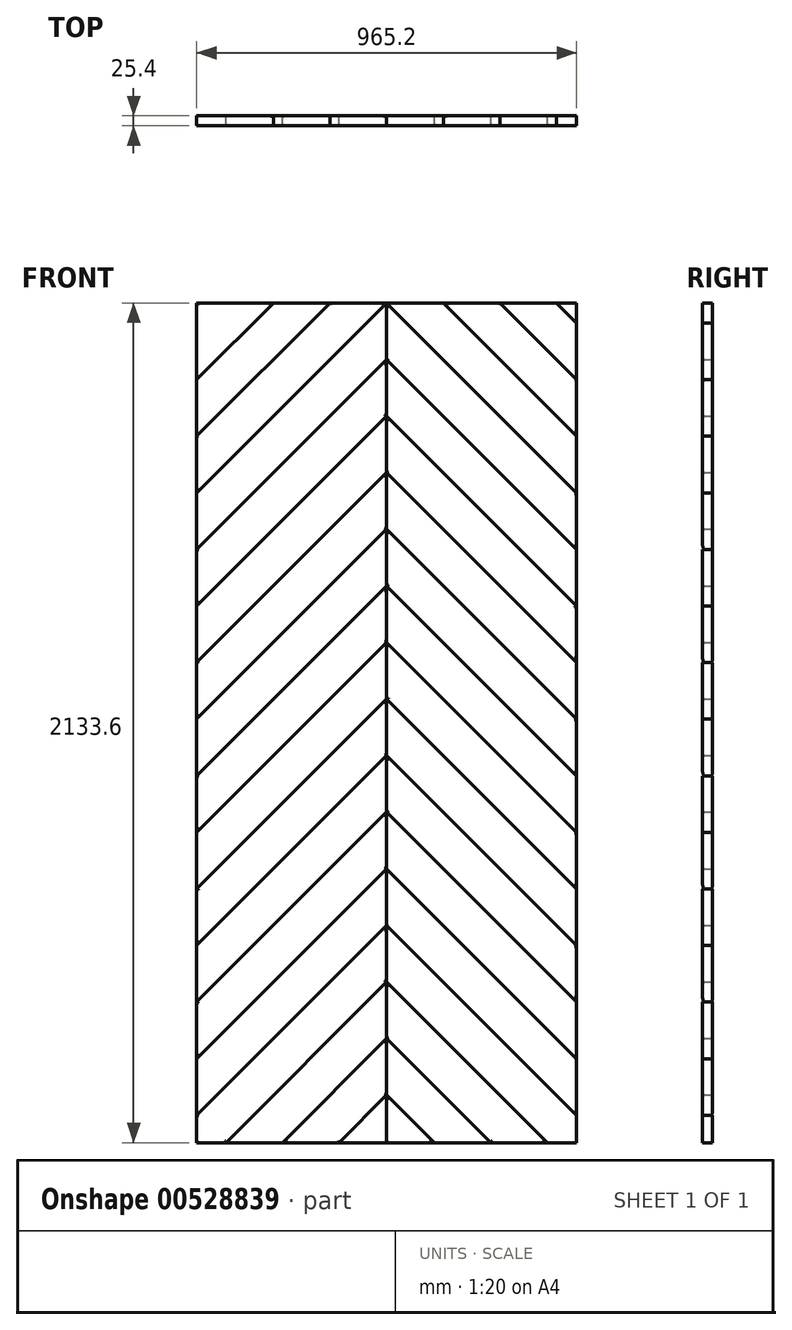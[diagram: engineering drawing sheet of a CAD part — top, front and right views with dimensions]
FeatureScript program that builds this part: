
annotation { "Feature Type Name" : "Feature", "Feature Type Description" : "" }
export const myFeature = defineFeature(function(context is Context, id is Id, definition is map)
    precondition{}
    {
        {
            var Q0;
            Q0=qCreatedBy(makeId("Front.planeOp"),FACE);
            var sketch = newSketch(context, id + "F0", { "sketchPlane" : qUnion([Q0])});
            skLineSegment(sketch, "E0.bottom", {"start": v(482.6, -1066.8) * mm, "end": v(0, -1066.8) * mm});
            skLineSegment(sketch, "E0.top", {"start": v(482.6, 1066.8) * mm, "end": v(0, 1066.8) * mm});
            skLineSegment(sketch, "E0.left", {"start": v(482.6, -1066.8) * mm, "end": v(482.6, 1066.8) * mm});
            skLineSegment(sketch, "E0.right", {"start": v(-482.6, -1066.8) * mm, "end": v(-482.6, 1066.8) * mm});
            skPoint(sketch, "E0.middle", {"position": v(0, 0) * mm});
            skLineSegment(sketch, "E1", {"start": v(0, 1066.8) * mm, "end": v(-482.6, 1066.8) * mm});
            skLineSegment(sketch, "E2", {"start": v(0, -1066.8) * mm, "end": v(-482.6, -1066.8) * mm});
            skLineSegment(sketch, "E3", {"start": v(0, 1066.8) * mm, "end": v(0, -1066.8) * mm});
            skLineSegment(sketch, "E4", {"start": v(0, 1066.8) * mm, "end": v(-482.6, 584.2) * mm});
            skLineSegment(sketch, "E5.1.0.0", {"start": v(0, 923.04) * mm, "end": v(-482.6, 440.44) * mm});
            skLineSegment(sketch, "E5.2.0.0", {"start": v(0, 779.27) * mm, "end": v(-482.6, 296.67) * mm});
            skLineSegment(sketch, "E5.3.0.0", {"start": v(0, 635.5) * mm, "end": v(-482.6, 152.9) * mm});
            skLineSegment(sketch, "E5.4.0.0", {"start": v(0, 491.74) * mm, "end": v(-482.6, 9.14) * mm});
            skLineSegment(sketch, "E5.5.0.0", {"start": v(0, 347.98) * mm, "end": v(-482.6, -134.62) * mm});
            skLineSegment(sketch, "E5.6.0.0", {"start": v(0, 204.22) * mm, "end": v(-482.6, -278.38) * mm});
            skLineSegment(sketch, "E5.7.0.0", {"start": v(0, 60.45) * mm, "end": v(-482.6, -422.15) * mm});
            skLineSegment(sketch, "E5.8.0.0", {"start": v(0, -83.31) * mm, "end": v(-482.6, -565.91) * mm});
            skLineSegment(sketch, "E5.9.0.0", {"start": v(0, -227.08) * mm, "end": v(-482.6, -709.68) * mm});
            skLineSegment(sketch, "E5.10.0.0", {"start": v(0, -370.84) * mm, "end": v(-482.6, -853.44) * mm});
            skLineSegment(sketch, "E5.11.0.0", {"start": v(0, -514.6) * mm, "end": v(-482.6, -997.2) * mm});
            skLineSegment(sketch, "E5.12.0.0", {"start": v(0, -658.37) * mm, "end": v(-408.43, -1066.8) * mm});
            skLineSegment(sketch, "E5.13.0.0", {"start": v(0, -802.13) * mm, "end": v(-264.67, -1066.8) * mm});
            skLineSegment(sketch, "E5.14.0.0", {"start": v(0, -945.9) * mm, "end": v(-120.9, -1066.8) * mm});
            skLineSegment(sketch, "E5.direction1", {"start": v(-482.6, 584.2) * mm, "end": v(-482.6, 440.44) * mm, "construction": true});
            skPoint(sketch, "E6.orphan", {"position": v(-482.6, -1428.5) * mm});
            skPoint(sketch, "E7.orphan", {"position": v(-482.6, -1284.73) * mm});
            skPoint(sketch, "E8.orphan", {"position": v(-482.6, -1140.97) * mm});
            skLineSegment(sketch, "E9.1.0.0", {"start": v(-143.76, 1066.8) * mm, "end": v(-482.6, 727.96) * mm});
            skLineSegment(sketch, "E9.2.0.0", {"start": v(-287.53, 1066.8) * mm, "end": v(-482.6, 871.73) * mm});
            skLineSegment(sketch, "E9.3.0.0", {"start": v(-431.3, 1066.8) * mm, "end": v(-482.6, 1015.5) * mm});
            skLineSegment(sketch, "E9.direction1", {"start": v(-482.6, 584.2) * mm, "end": v(-626.36, 584.2) * mm, "construction": true});
            skPoint(sketch, "E10.orphan", {"position": v(-913.9, 584.2) * mm});
            skPoint(sketch, "E11.orphan", {"position": v(-770.13, 584.2) * mm});
            skLineSegment(sketch, "E12", {"start": v(0, 1066.8) * mm, "end": v(482.6, 584.2) * mm});
            skLineSegment(sketch, "E13.1.0.0", {"start": v(143.76, 1066.8) * mm, "end": v(482.6, 727.96) * mm});
            skLineSegment(sketch, "E13.2.0.0", {"start": v(287.53, 1066.8) * mm, "end": v(482.6, 871.73) * mm});
            skLineSegment(sketch, "E13.3.0.0", {"start": v(431.3, 1066.8) * mm, "end": v(482.6, 1015.5) * mm});
            skLineSegment(sketch, "E13.direction1", {"start": v(0, 1066.8) * mm, "end": v(143.76, 1066.8) * mm, "construction": true});
            skPoint(sketch, "E14.orphan", {"position": v(913.9, 584.2) * mm});
            skPoint(sketch, "E15.orphan", {"position": v(770.13, 584.2) * mm});
            skPoint(sketch, "E16.orphan", {"position": v(626.36, 584.2) * mm});
            skLineSegment(sketch, "E17.1.0.0", {"start": v(0, 923.04) * mm, "end": v(482.6, 440.44) * mm});
            skLineSegment(sketch, "E17.2.0.0", {"start": v(0, 779.27) * mm, "end": v(482.6, 296.67) * mm});
            skLineSegment(sketch, "E17.3.0.0", {"start": v(0, 635.5) * mm, "end": v(482.6, 152.9) * mm});
            skLineSegment(sketch, "E17.4.0.0", {"start": v(0, 491.74) * mm, "end": v(482.6, 9.14) * mm});
            skLineSegment(sketch, "E17.5.0.0", {"start": v(0, 347.98) * mm, "end": v(482.6, -134.62) * mm});
            skLineSegment(sketch, "E17.6.0.0", {"start": v(0, 204.22) * mm, "end": v(482.6, -278.38) * mm});
            skLineSegment(sketch, "E17.7.0.0", {"start": v(0, 60.45) * mm, "end": v(482.6, -422.15) * mm});
            skLineSegment(sketch, "E17.8.0.0", {"start": v(0, -83.31) * mm, "end": v(482.6, -565.91) * mm});
            skLineSegment(sketch, "E17.9.0.0", {"start": v(0, -227.08) * mm, "end": v(482.6, -709.68) * mm});
            skLineSegment(sketch, "E17.10.0.0", {"start": v(0, -370.84) * mm, "end": v(482.6, -853.44) * mm});
            skLineSegment(sketch, "E17.11.0.0", {"start": v(0, -514.6) * mm, "end": v(482.6, -997.2) * mm});
            skLineSegment(sketch, "E17.12.0.0", {"start": v(0, -658.37) * mm, "end": v(408.43, -1066.8) * mm});
            skLineSegment(sketch, "E17.13.0.0", {"start": v(0, -802.13) * mm, "end": v(264.67, -1066.8) * mm});
            skLineSegment(sketch, "E17.14.0.0", {"start": v(0, -945.9) * mm, "end": v(120.9, -1066.8) * mm});
            skLineSegment(sketch, "E17.direction1", {"start": v(0, 1066.8) * mm, "end": v(0, 923.04) * mm, "construction": true});
            skPoint(sketch, "E18.orphan", {"position": v(482.6, -1428.5) * mm});
            skPoint(sketch, "E19.orphan", {"position": v(482.6, -1284.73) * mm});
            skPoint(sketch, "E20.orphan", {"position": v(482.6, -1140.97) * mm});
            skSolve(sketch);
        }
        {
            var Q0;
            {var subQ3=sQuery(id+"F0.wireOp",EDGE,"E9.3.0.0");Q0=makeQuery(id+"F0.imprint","IMPRINT",FACE,{"disambiguationData":[TD([[makeQuery(id+"F0.imprint","IMPRINT",EDGE,{"derivedFrom":subQ3}),-1.0]])]});}
            var Q1;
            {var subQ3=sQuery(id+"F0.wireOp",EDGE,"E13.3.0.0");Q1=makeQuery(id+"F0.imprint","IMPRINT",FACE,{"disambiguationData":[TD([[makeQuery(id+"F0.imprint","IMPRINT",EDGE,{"derivedFrom":subQ3}),1.0]])]});}
            var Q2;
            {var subQ3=sQuery(id+"F0.wireOp",EDGE,"E17.14.0.0");Q2=makeQuery(id+"F0.imprint","IMPRINT",FACE,{"disambiguationData":[TD([[makeQuery(id+"F0.imprint","IMPRINT",EDGE,{"derivedFrom":subQ3}),-1.0]])]});}
            var Q3;
            {var subQ0=sQuery(id+"F0.wireOp",EDGE,"E5.13.0.0");Q3=makeQuery(id+"F0.imprint","IMPRINT",FACE,{"disambiguationData":[TD([[makeQuery(id+"F0.imprint","IMPRINT",EDGE,{"derivedFrom":subQ0}),1.0]])]});}
            var Q4;
            {var subQ0=sQuery(id+"F0.wireOp",EDGE,"E17.12.0.0");Q4=makeQuery(id+"F0.imprint","IMPRINT",FACE,{"disambiguationData":[TD([[makeQuery(id+"F0.imprint","IMPRINT",EDGE,{"derivedFrom":subQ0}),-1.0]])]});}
            var Q5;
            {var subQ4=sQuery(id+"F0.wireOp",EDGE,"E5.11.0.0");Q5=makeQuery(id+"F0.imprint","IMPRINT",FACE,{"disambiguationData":[TD([[makeQuery(id+"F0.imprint","IMPRINT",EDGE,{"derivedFrom":subQ4}),1.0]])]});}
            var Q6;
            {var subQ0=sQuery(id+"F0.wireOp",EDGE,"E17.10.0.0");Q6=makeQuery(id+"F0.imprint","IMPRINT",FACE,{"disambiguationData":[TD([[makeQuery(id+"F0.imprint","IMPRINT",EDGE,{"derivedFrom":subQ0}),-1.0]])]});}
            var Q7;
            {var subQ0=sQuery(id+"F0.wireOp",EDGE,"E5.9.0.0");Q7=makeQuery(id+"F0.imprint","IMPRINT",FACE,{"disambiguationData":[TD([[makeQuery(id+"F0.imprint","IMPRINT",EDGE,{"derivedFrom":subQ0}),1.0]])]});}
            var Q8;
            {var subQ0=sQuery(id+"F0.wireOp",EDGE,"E17.8.0.0");Q8=makeQuery(id+"F0.imprint","IMPRINT",FACE,{"disambiguationData":[TD([[makeQuery(id+"F0.imprint","IMPRINT",EDGE,{"derivedFrom":subQ0}),-1.0]])]});}
            var Q9;
            {var subQ0=sQuery(id+"F0.wireOp",EDGE,"E5.7.0.0");Q9=makeQuery(id+"F0.imprint","IMPRINT",FACE,{"disambiguationData":[TD([[makeQuery(id+"F0.imprint","IMPRINT",EDGE,{"derivedFrom":subQ0}),1.0]])]});}
            var Q10;
            {var subQ0=sQuery(id+"F0.wireOp",EDGE,"E17.6.0.0");Q10=makeQuery(id+"F0.imprint","IMPRINT",FACE,{"disambiguationData":[TD([[makeQuery(id+"F0.imprint","IMPRINT",EDGE,{"derivedFrom":subQ0}),-1.0]])]});}
            var Q11;
            {var subQ0=sQuery(id+"F0.wireOp",EDGE,"E5.5.0.0");Q11=makeQuery(id+"F0.imprint","IMPRINT",FACE,{"disambiguationData":[TD([[makeQuery(id+"F0.imprint","IMPRINT",EDGE,{"derivedFrom":subQ0}),1.0]])]});}
            var Q12;
            {var subQ0=sQuery(id+"F0.wireOp",EDGE,"E17.4.0.0");Q12=makeQuery(id+"F0.imprint","IMPRINT",FACE,{"disambiguationData":[TD([[makeQuery(id+"F0.imprint","IMPRINT",EDGE,{"derivedFrom":subQ0}),-1.0]])]});}
            var Q13;
            {var subQ0=sQuery(id+"F0.wireOp",EDGE,"E5.3.0.0");Q13=makeQuery(id+"F0.imprint","IMPRINT",FACE,{"disambiguationData":[TD([[makeQuery(id+"F0.imprint","IMPRINT",EDGE,{"derivedFrom":subQ0}),1.0]])]});}
            var Q14;
            {var subQ0=sQuery(id+"F0.wireOp",EDGE,"E17.2.0.0");Q14=makeQuery(id+"F0.imprint","IMPRINT",FACE,{"disambiguationData":[TD([[makeQuery(id+"F0.imprint","IMPRINT",EDGE,{"derivedFrom":subQ0}),-1.0]])]});}
            var Q15;
            {var subQ0=sQuery(id+"F0.wireOp",EDGE,"E5.1.0.0");Q15=makeQuery(id+"F0.imprint","IMPRINT",FACE,{"disambiguationData":[TD([[makeQuery(id+"F0.imprint","IMPRINT",EDGE,{"derivedFrom":subQ0}),1.0]])]});}
            var Q16;
            {var subQ0=sQuery(id+"F0.wireOp",EDGE,"E12");Q16=makeQuery(id+"F0.imprint","IMPRINT",FACE,{"disambiguationData":[TD([[makeQuery(id+"F0.imprint","IMPRINT",EDGE,{"derivedFrom":subQ0}),-1.0]])]});}
            var Q17;
            {var subQ0=sQuery(id+"F0.wireOp",EDGE,"E4");Q17=makeQuery(id+"F0.imprint","IMPRINT",FACE,{"disambiguationData":[TD([[makeQuery(id+"F0.imprint","IMPRINT",EDGE,{"derivedFrom":subQ0}),-1.0]])]});}
            var Q18;
            {var subQ0=sQuery(id+"F0.wireOp",EDGE,"E13.1.0.0");Q18=makeQuery(id+"F0.imprint","IMPRINT",FACE,{"disambiguationData":[TD([[makeQuery(id+"F0.imprint","IMPRINT",EDGE,{"derivedFrom":subQ0}),1.0]])]});}
            var Q19;
            {var subQ0=sQuery(id+"F0.wireOp",EDGE,"E9.2.0.0");Q19=makeQuery(id+"F0.imprint","IMPRINT",FACE,{"disambiguationData":[TD([[makeQuery(id+"F0.imprint","IMPRINT",EDGE,{"derivedFrom":subQ0}),-1.0]])]});}
            extrude(context, id + "F1", {"entities" : qUnion([Q0, Q1, Q2, Q3, Q4, Q5, Q6, Q7, Q8, Q9, Q10, Q11, Q12, Q13, Q14, Q15, Q16, Q17, Q18, Q19]), "depth" : 25.4 * mm, "offsetDistance" : 25.4 * mm});
        }
        {
            var Q0;
            Q0=makeQuery(id+"F1.opExtrude","CAP_EDGE",EDGE,{"disambiguationData":[OSD([sQuery(id+"F0.wireOp",EDGE,"E9.2.0.0")])],"isStart":false});
            var Q1;
            Q1=makeQuery(id+"F1.opExtrude","CAP_EDGE",EDGE,{"disambiguationData":[OSD([sQuery(id+"F0.wireOp",EDGE,"E9.1.0.0")])],"isStart":true});
            var Q2;
            Q2=makeQuery(id+"F1.opExtrude","CAP_EDGE",EDGE,{"disambiguationData":[OSD([sQuery(id+"F0.wireOp",EDGE,"E4")])],"isStart":false});
            var Q3;
            {var subQ0=sQuery(id+"F0.wireOp",EDGE,"E3");Q3=makeQuery(id+"F1.opExtrude","CAP_EDGE",EDGE,{"disambiguationData":[OSD([subQ0]),TDD([makeQuery(id+"F0.imprint","IMPRINT",EDGE,{"disambiguationData":[TD([[makeQuery(id+"F0.imprint","INTERSECT",VERTEX,{"derivedFrom":[subQ0,sQuery(id+"F0.wireOp",EDGE,"E5.1.0.0"),sQuery(id+"F0.wireOp",EDGE,"E17.1.0.0")]}),1.0]])],"derivedFrom":subQ0})])],"isStart":true});}
            var Q4;
            Q4=makeQuery(id+"F1.opExtrude","CAP_EDGE",EDGE,{"disambiguationData":[OSD([sQuery(id+"F0.wireOp",EDGE,"E13.2.0.0")])],"isStart":false});
            var Q5;
            Q5=makeQuery(id+"F1.opExtrude","CAP_EDGE",EDGE,{"disambiguationData":[OSD([sQuery(id+"F0.wireOp",EDGE,"E13.1.0.0")])],"isStart":true});
            var Q6;
            Q6=makeQuery(id+"F1.opExtrude","CAP_EDGE",EDGE,{"disambiguationData":[OSD([sQuery(id+"F0.wireOp",EDGE,"E12")])],"isStart":false});
            var Q7;
            Q7=makeQuery(id+"F1.opExtrude","CAP_FACE",FACE,{"disambiguationData":[OSD([sQuery(id+"F0.wireOp",EDGE,"E0.left"),sQuery(id+"F0.wireOp",EDGE,"E3"),sQuery(id+"F0.wireOp",EDGE,"E12"),sQuery(id+"F0.wireOp",EDGE,"E17.1.0.0")])],"isStart":false});
            var Q8;
            Q8=makeQuery(id+"F1.opExtrude","CAP_FACE",FACE,{"disambiguationData":[OSD([sQuery(id+"F0.wireOp",EDGE,"E0.left"),sQuery(id+"F0.wireOp",EDGE,"E3"),sQuery(id+"F0.wireOp",EDGE,"E17.2.0.0"),sQuery(id+"F0.wireOp",EDGE,"E17.3.0.0")])],"isStart":false});
            var Q9;
            Q9=makeQuery(id+"F1.opExtrude","CAP_FACE",FACE,{"disambiguationData":[OSD([sQuery(id+"F0.wireOp",EDGE,"E0.right"),sQuery(id+"F0.wireOp",EDGE,"E3"),sQuery(id+"F0.wireOp",EDGE,"E5.1.0.0"),sQuery(id+"F0.wireOp",EDGE,"E5.2.0.0")])],"isStart":false});
            var Q10;
            Q10=makeQuery(id+"F1.opExtrude","CAP_FACE",FACE,{"disambiguationData":[OSD([sQuery(id+"F0.wireOp",EDGE,"E0.right"),sQuery(id+"F0.wireOp",EDGE,"E3"),sQuery(id+"F0.wireOp",EDGE,"E5.3.0.0"),sQuery(id+"F0.wireOp",EDGE,"E5.4.0.0")])],"isStart":false});
            var Q11;
            Q11=makeQuery(id+"F1.opExtrude","CAP_FACE",FACE,{"disambiguationData":[OSD([sQuery(id+"F0.wireOp",EDGE,"E0.left"),sQuery(id+"F0.wireOp",EDGE,"E3"),sQuery(id+"F0.wireOp",EDGE,"E17.4.0.0"),sQuery(id+"F0.wireOp",EDGE,"E17.5.0.0")])],"isStart":false});
            var Q12;
            Q12=makeQuery(id+"F1.opExtrude","CAP_FACE",FACE,{"disambiguationData":[OSD([sQuery(id+"F0.wireOp",EDGE,"E0.left"),sQuery(id+"F0.wireOp",EDGE,"E3"),sQuery(id+"F0.wireOp",EDGE,"E17.6.0.0"),sQuery(id+"F0.wireOp",EDGE,"E17.7.0.0")])],"isStart":false});
            var Q13;
            Q13=makeQuery(id+"F1.opExtrude","CAP_FACE",FACE,{"disambiguationData":[OSD([sQuery(id+"F0.wireOp",EDGE,"E0.right"),sQuery(id+"F0.wireOp",EDGE,"E3"),sQuery(id+"F0.wireOp",EDGE,"E5.5.0.0"),sQuery(id+"F0.wireOp",EDGE,"E5.6.0.0")])],"isStart":false});
            var Q14;
            Q14=makeQuery(id+"F1.opExtrude","CAP_FACE",FACE,{"disambiguationData":[OSD([sQuery(id+"F0.wireOp",EDGE,"E0.right"),sQuery(id+"F0.wireOp",EDGE,"E3"),sQuery(id+"F0.wireOp",EDGE,"E5.7.0.0"),sQuery(id+"F0.wireOp",EDGE,"E5.8.0.0")])],"isStart":false});
            var Q15;
            Q15=makeQuery(id+"F1.opExtrude","CAP_FACE",FACE,{"disambiguationData":[OSD([sQuery(id+"F0.wireOp",EDGE,"E0.left"),sQuery(id+"F0.wireOp",EDGE,"E3"),sQuery(id+"F0.wireOp",EDGE,"E17.8.0.0"),sQuery(id+"F0.wireOp",EDGE,"E17.9.0.0")])],"isStart":false});
            var Q16;
            Q16=makeQuery(id+"F1.opExtrude","CAP_FACE",FACE,{"disambiguationData":[OSD([sQuery(id+"F0.wireOp",EDGE,"E0.right"),sQuery(id+"F0.wireOp",EDGE,"E3"),sQuery(id+"F0.wireOp",EDGE,"E5.9.0.0"),sQuery(id+"F0.wireOp",EDGE,"E5.10.0.0")])],"isStart":false});
            var Q17;
            Q17=makeQuery(id+"F1.opExtrude","CAP_FACE",FACE,{"disambiguationData":[OSD([sQuery(id+"F0.wireOp",EDGE,"E0.right"),sQuery(id+"F0.wireOp",EDGE,"E2"),sQuery(id+"F0.wireOp",EDGE,"E3"),sQuery(id+"F0.wireOp",EDGE,"E5.11.0.0"),sQuery(id+"F0.wireOp",EDGE,"E5.12.0.0")])],"isStart":false});
            var Q18;
            Q18=makeQuery(id+"F1.opExtrude","CAP_FACE",FACE,{"disambiguationData":[OSD([sQuery(id+"F0.wireOp",EDGE,"E2"),sQuery(id+"F0.wireOp",EDGE,"E3"),sQuery(id+"F0.wireOp",EDGE,"E5.13.0.0"),sQuery(id+"F0.wireOp",EDGE,"E5.14.0.0")])],"isStart":false});
            var Q19;
            Q19=makeQuery(id+"F1.opExtrude","CAP_FACE",FACE,{"disambiguationData":[OSD([sQuery(id+"F0.wireOp",EDGE,"E0.bottom"),sQuery(id+"F0.wireOp",EDGE,"E3"),sQuery(id+"F0.wireOp",EDGE,"E17.12.0.0"),sQuery(id+"F0.wireOp",EDGE,"E17.13.0.0")])],"isStart":false});
            var Q20;
            Q20=makeQuery(id+"F1.opExtrude","CAP_FACE",FACE,{"disambiguationData":[OSD([sQuery(id+"F0.wireOp",EDGE,"E0.bottom"),sQuery(id+"F0.wireOp",EDGE,"E3"),sQuery(id+"F0.wireOp",EDGE,"E17.14.0.0")])],"isStart":false});
            var Q21;
            Q21=makeQuery(id+"F1.opExtrude","CAP_FACE",FACE,{"disambiguationData":[OSD([sQuery(id+"F0.wireOp",EDGE,"E0.right"),sQuery(id+"F0.wireOp",EDGE,"E3"),sQuery(id+"F0.wireOp",EDGE,"E5.1.0.0"),sQuery(id+"F0.wireOp",EDGE,"E5.2.0.0")])],"isStart":true});
            var Q22;
            Q22=makeQuery(id+"F1.opExtrude","CAP_FACE",FACE,{"disambiguationData":[OSD([sQuery(id+"F0.wireOp",EDGE,"E0.right"),sQuery(id+"F0.wireOp",EDGE,"E1"),sQuery(id+"F0.wireOp",EDGE,"E9.2.0.0")])],"isStart":true});
            var Q23;
            Q23=makeQuery(id+"F1.opExtrude","CAP_FACE",FACE,{"disambiguationData":[OSD([sQuery(id+"F0.wireOp",EDGE,"E0.right"),sQuery(id+"F0.wireOp",EDGE,"E1"),sQuery(id+"F0.wireOp",EDGE,"E4"),sQuery(id+"F0.wireOp",EDGE,"E9.1.0.0")])],"isStart":true});
            var Q24;
            Q24=makeQuery(id+"F1.opExtrude","CAP_FACE",FACE,{"disambiguationData":[OSD([sQuery(id+"F0.wireOp",EDGE,"E0.right"),sQuery(id+"F0.wireOp",EDGE,"E3"),sQuery(id+"F0.wireOp",EDGE,"E5.3.0.0"),sQuery(id+"F0.wireOp",EDGE,"E5.4.0.0")])],"isStart":true});
            var Q25;
            Q25=makeQuery(id+"F1.opExtrude","CAP_FACE",FACE,{"disambiguationData":[OSD([sQuery(id+"F0.wireOp",EDGE,"E0.right"),sQuery(id+"F0.wireOp",EDGE,"E3"),sQuery(id+"F0.wireOp",EDGE,"E5.5.0.0"),sQuery(id+"F0.wireOp",EDGE,"E5.6.0.0")])],"isStart":true});
            var Q26;
            Q26=makeQuery(id+"F1.opExtrude","CAP_FACE",FACE,{"disambiguationData":[OSD([sQuery(id+"F0.wireOp",EDGE,"E0.right"),sQuery(id+"F0.wireOp",EDGE,"E3"),sQuery(id+"F0.wireOp",EDGE,"E5.7.0.0"),sQuery(id+"F0.wireOp",EDGE,"E5.8.0.0")])],"isStart":true});
            var Q27;
            Q27=makeQuery(id+"F1.opExtrude","CAP_FACE",FACE,{"disambiguationData":[OSD([sQuery(id+"F0.wireOp",EDGE,"E0.top"),sQuery(id+"F0.wireOp",EDGE,"E0.left"),sQuery(id+"F0.wireOp",EDGE,"E13.1.0.0"),sQuery(id+"F0.wireOp",EDGE,"E13.2.0.0")])],"isStart":true});
            var Q28;
            Q28=makeQuery(id+"F1.opExtrude","CAP_FACE",FACE,{"disambiguationData":[OSD([sQuery(id+"F0.wireOp",EDGE,"E0.left"),sQuery(id+"F0.wireOp",EDGE,"E3"),sQuery(id+"F0.wireOp",EDGE,"E12"),sQuery(id+"F0.wireOp",EDGE,"E17.1.0.0")])],"isStart":true});
            var Q29;
            Q29=makeQuery(id+"F1.opExtrude","CAP_FACE",FACE,{"disambiguationData":[OSD([sQuery(id+"F0.wireOp",EDGE,"E0.left"),sQuery(id+"F0.wireOp",EDGE,"E3"),sQuery(id+"F0.wireOp",EDGE,"E17.2.0.0"),sQuery(id+"F0.wireOp",EDGE,"E17.3.0.0")])],"isStart":true});
            var Q30;
            Q30=makeQuery(id+"F1.opExtrude","CAP_FACE",FACE,{"disambiguationData":[OSD([sQuery(id+"F0.wireOp",EDGE,"E0.left"),sQuery(id+"F0.wireOp",EDGE,"E3"),sQuery(id+"F0.wireOp",EDGE,"E17.4.0.0"),sQuery(id+"F0.wireOp",EDGE,"E17.5.0.0")])],"isStart":true});
            var Q31;
            Q31=makeQuery(id+"F1.opExtrude","CAP_FACE",FACE,{"disambiguationData":[OSD([sQuery(id+"F0.wireOp",EDGE,"E0.left"),sQuery(id+"F0.wireOp",EDGE,"E3"),sQuery(id+"F0.wireOp",EDGE,"E17.6.0.0"),sQuery(id+"F0.wireOp",EDGE,"E17.7.0.0")])],"isStart":true});
            var Q32;
            Q32=makeQuery(id+"F1.opExtrude","CAP_FACE",FACE,{"disambiguationData":[OSD([sQuery(id+"F0.wireOp",EDGE,"E0.left"),sQuery(id+"F0.wireOp",EDGE,"E3"),sQuery(id+"F0.wireOp",EDGE,"E17.8.0.0"),sQuery(id+"F0.wireOp",EDGE,"E17.9.0.0")])],"isStart":true});
            var Q33;
            Q33=makeQuery(id+"F1.opExtrude","CAP_FACE",FACE,{"disambiguationData":[OSD([sQuery(id+"F0.wireOp",EDGE,"E0.right"),sQuery(id+"F0.wireOp",EDGE,"E3"),sQuery(id+"F0.wireOp",EDGE,"E5.9.0.0"),sQuery(id+"F0.wireOp",EDGE,"E5.10.0.0")])],"isStart":true});
            var Q34;
            Q34=makeQuery(id+"F1.opExtrude","CAP_FACE",FACE,{"disambiguationData":[OSD([sQuery(id+"F0.wireOp",EDGE,"E0.left"),sQuery(id+"F0.wireOp",EDGE,"E3"),sQuery(id+"F0.wireOp",EDGE,"E17.10.0.0"),sQuery(id+"F0.wireOp",EDGE,"E17.11.0.0")])],"isStart":true});
            var Q35;
            Q35=makeQuery(id+"F1.opExtrude","CAP_FACE",FACE,{"disambiguationData":[OSD([sQuery(id+"F0.wireOp",EDGE,"E0.right"),sQuery(id+"F0.wireOp",EDGE,"E2"),sQuery(id+"F0.wireOp",EDGE,"E3"),sQuery(id+"F0.wireOp",EDGE,"E5.11.0.0"),sQuery(id+"F0.wireOp",EDGE,"E5.12.0.0")])],"isStart":true});
            var Q36;
            Q36=makeQuery(id+"F1.opExtrude","CAP_FACE",FACE,{"disambiguationData":[OSD([sQuery(id+"F0.wireOp",EDGE,"E0.bottom"),sQuery(id+"F0.wireOp",EDGE,"E3"),sQuery(id+"F0.wireOp",EDGE,"E17.12.0.0"),sQuery(id+"F0.wireOp",EDGE,"E17.13.0.0")])],"isStart":true});
            var Q37;
            Q37=makeQuery(id+"F1.opExtrude","CAP_FACE",FACE,{"disambiguationData":[OSD([sQuery(id+"F0.wireOp",EDGE,"E2"),sQuery(id+"F0.wireOp",EDGE,"E3"),sQuery(id+"F0.wireOp",EDGE,"E5.13.0.0"),sQuery(id+"F0.wireOp",EDGE,"E5.14.0.0")])],"isStart":true});
            var Q38;
            Q38=makeQuery(id+"F1.opExtrude","CAP_FACE",FACE,{"disambiguationData":[OSD([sQuery(id+"F0.wireOp",EDGE,"E0.bottom"),sQuery(id+"F0.wireOp",EDGE,"E3"),sQuery(id+"F0.wireOp",EDGE,"E17.14.0.0")])],"isStart":true});
            fillet(context, id + "F2", {"entities" : qUnion([Q0, Q1, Q2, Q3, Q4, Q5, Q6, Q7, Q8, Q9, Q10, Q11, Q12, Q13, Q14, Q15, Q16, Q17, Q18, Q19, Q20, Q21, Q22, Q23, Q24, Q25, Q26, Q27, Q28, Q29, Q30, Q31, Q32, Q33, Q34, Q35, Q36, Q37, Q38]), "radius" : 5.08 * mm, "tangentPropagation" : true, "allowEdgeOverflow" : false});
        }
        {
            var Q0;
            {var subQ3=sQuery(id+"F0.wireOp",EDGE,"E5.14.0.0");Q0=makeQuery(id+"F0.imprint","IMPRINT",FACE,{"disambiguationData":[TD([[makeQuery(id+"F0.imprint","IMPRINT",EDGE,{"derivedFrom":subQ3}),1.0]])]});}
            var Q1;
            {var subQ0=sQuery(id+"F0.wireOp",EDGE,"E5.12.0.0");Q1=makeQuery(id+"F0.imprint","IMPRINT",FACE,{"disambiguationData":[TD([[makeQuery(id+"F0.imprint","IMPRINT",EDGE,{"derivedFrom":subQ0}),1.0]])]});}
            var Q2;
            {var subQ0=sQuery(id+"F0.wireOp",EDGE,"E17.13.0.0");Q2=makeQuery(id+"F0.imprint","IMPRINT",FACE,{"disambiguationData":[TD([[makeQuery(id+"F0.imprint","IMPRINT",EDGE,{"derivedFrom":subQ0}),-1.0]])]});}
            var Q3;
            {var subQ0=sQuery(id+"F0.wireOp",EDGE,"E17.11.0.0");Q3=makeQuery(id+"F0.imprint","IMPRINT",FACE,{"disambiguationData":[TD([[makeQuery(id+"F0.imprint","IMPRINT",EDGE,{"derivedFrom":subQ0}),-1.0]])]});}
            var Q4;
            {var subQ0=sQuery(id+"F0.wireOp",EDGE,"E17.9.0.0");Q4=makeQuery(id+"F0.imprint","IMPRINT",FACE,{"disambiguationData":[TD([[makeQuery(id+"F0.imprint","IMPRINT",EDGE,{"derivedFrom":subQ0}),-1.0]])]});}
            var Q5;
            {var subQ0=sQuery(id+"F0.wireOp",EDGE,"E5.10.0.0");Q5=makeQuery(id+"F0.imprint","IMPRINT",FACE,{"disambiguationData":[TD([[makeQuery(id+"F0.imprint","IMPRINT",EDGE,{"derivedFrom":subQ0}),1.0]])]});}
            var Q6;
            {var subQ0=sQuery(id+"F0.wireOp",EDGE,"E5.8.0.0");Q6=makeQuery(id+"F0.imprint","IMPRINT",FACE,{"disambiguationData":[TD([[makeQuery(id+"F0.imprint","IMPRINT",EDGE,{"derivedFrom":subQ0}),1.0]])]});}
            var Q7;
            {var subQ0=sQuery(id+"F0.wireOp",EDGE,"E5.6.0.0");Q7=makeQuery(id+"F0.imprint","IMPRINT",FACE,{"disambiguationData":[TD([[makeQuery(id+"F0.imprint","IMPRINT",EDGE,{"derivedFrom":subQ0}),1.0]])]});}
            var Q8;
            {var subQ0=sQuery(id+"F0.wireOp",EDGE,"E17.7.0.0");Q8=makeQuery(id+"F0.imprint","IMPRINT",FACE,{"disambiguationData":[TD([[makeQuery(id+"F0.imprint","IMPRINT",EDGE,{"derivedFrom":subQ0}),-1.0]])]});}
            var Q9;
            {var subQ0=sQuery(id+"F0.wireOp",EDGE,"E17.5.0.0");Q9=makeQuery(id+"F0.imprint","IMPRINT",FACE,{"disambiguationData":[TD([[makeQuery(id+"F0.imprint","IMPRINT",EDGE,{"derivedFrom":subQ0}),-1.0]])]});}
            var Q10;
            {var subQ0=sQuery(id+"F0.wireOp",EDGE,"E5.4.0.0");Q10=makeQuery(id+"F0.imprint","IMPRINT",FACE,{"disambiguationData":[TD([[makeQuery(id+"F0.imprint","IMPRINT",EDGE,{"derivedFrom":subQ0}),1.0]])]});}
            var Q11;
            {var subQ0=sQuery(id+"F0.wireOp",EDGE,"E17.3.0.0");Q11=makeQuery(id+"F0.imprint","IMPRINT",FACE,{"disambiguationData":[TD([[makeQuery(id+"F0.imprint","IMPRINT",EDGE,{"derivedFrom":subQ0}),-1.0]])]});}
            var Q12;
            {var subQ0=sQuery(id+"F0.wireOp",EDGE,"E5.2.0.0");Q12=makeQuery(id+"F0.imprint","IMPRINT",FACE,{"disambiguationData":[TD([[makeQuery(id+"F0.imprint","IMPRINT",EDGE,{"derivedFrom":subQ0}),1.0]])]});}
            var Q13;
            {var subQ0=sQuery(id+"F0.wireOp",EDGE,"E4");Q13=makeQuery(id+"F0.imprint","IMPRINT",FACE,{"disambiguationData":[TD([[makeQuery(id+"F0.imprint","IMPRINT",EDGE,{"derivedFrom":subQ0}),1.0]])]});}
            var Q14;
            {var subQ0=sQuery(id+"F0.wireOp",EDGE,"E17.1.0.0");Q14=makeQuery(id+"F0.imprint","IMPRINT",FACE,{"disambiguationData":[TD([[makeQuery(id+"F0.imprint","IMPRINT",EDGE,{"derivedFrom":subQ0}),-1.0]])]});}
            var Q15;
            {var subQ0=sQuery(id+"F0.wireOp",EDGE,"E12");Q15=makeQuery(id+"F0.imprint","IMPRINT",FACE,{"disambiguationData":[TD([[makeQuery(id+"F0.imprint","IMPRINT",EDGE,{"derivedFrom":subQ0}),1.0]])]});}
            var Q16;
            {var subQ0=sQuery(id+"F0.wireOp",EDGE,"E9.1.0.0");Q16=makeQuery(id+"F0.imprint","IMPRINT",FACE,{"disambiguationData":[TD([[makeQuery(id+"F0.imprint","IMPRINT",EDGE,{"derivedFrom":subQ0}),-1.0]])]});}
            var Q17;
            {var subQ0=sQuery(id+"F0.wireOp",EDGE,"E13.2.0.0");Q17=makeQuery(id+"F0.imprint","IMPRINT",FACE,{"disambiguationData":[TD([[makeQuery(id+"F0.imprint","IMPRINT",EDGE,{"derivedFrom":subQ0}),1.0]])]});}
            extrude(context, id + "F3", {"entities" : qUnion([Q0, Q1, Q2, Q3, Q4, Q5, Q6, Q7, Q8, Q9, Q10, Q11, Q12, Q13, Q14, Q15, Q16, Q17]), "depth" : 25.4 * mm, "offsetDistance" : 25.4 * mm});
        }
    });
